# Revit family: Mixer_Basin_Abey_Vela
name_source: partatom
category: Plumbing Fixtures
units: mm (PartAtom-declared; Revit-internal decimal feet)

## family parameters
Always vertical = Yes
Cut with Voids When Loaded = Yes
OmniClass Number = 23.31.11.19
Part Type = Normal
Room Calculation Point = No
Round Connector Dimension = Use Diameter
Shared = No
Work Plane-Based = No

## types (5) — shared parameters
Assembly Code = C1030210
Description = Manufactured from low-lead brass, the Vela Bathroom Collection will transform your bathroom into a sanctuary of grace, serenity and purification.
IfcExportAs = ifcValve
IfcExportType = FAUCET
Manufacturer = Abey
ManufacturerOverallDepth = 155 mm  [stored 0.50853 ft]
ManufacturerOverallHeight = 151 mm  [stored 0.495407 ft]
ManufacturerOverallWidth = 50 mm  [stored 0.164042 ft]
ManufacturerURLProductSpecific = https://www.abey.com.au
ModifiedIssue = 20230623 $
URL = https://www.abey.com.au
Uniclass2015Code = Pr_40_20_87_55
Uniclass2015Title = Mixer taps
Uniclass2015Version = Products v1.28
zero-valued in all types: Default Elevation

## per-type parameters (varying)
| type | BodyMaterial | CW Connection | HW Connection | ManufacturerSpecCode | Model | Type Comments |
| Chrome (7B1) | Metal_Abey_Chrome | No | No | 7B1 | 7B1 | Chrome |
| Black (7B1-B) | Metal_Abey_Black | No | No | 7B1-B | 7B1-B | Black |
| Brushed Nickel (7B1-BN) | Metal_Abey_BrushedNickel | No | No | 7B1-BN | 7B1-BN | Brushed Nickel |
| Gun Metal (7B1-GM) | Metal_Abey_GunMetal | No | No | 7B1-GM | 7B1-GM | Gun Metal |
| Brushed Brass (7B1-BB) | Metal_Abey_Brass | Yes | Yes | 7B1-BB | 7B1-BB | Brushed Brass |

note: [stored X ft] marks values corroborated as IEEE doubles in the binary element streams (Revit-internal decimal feet)

## geometry (parser evidence)
native form markers: Sweep x2
no freeform markers — native parametric forms only
